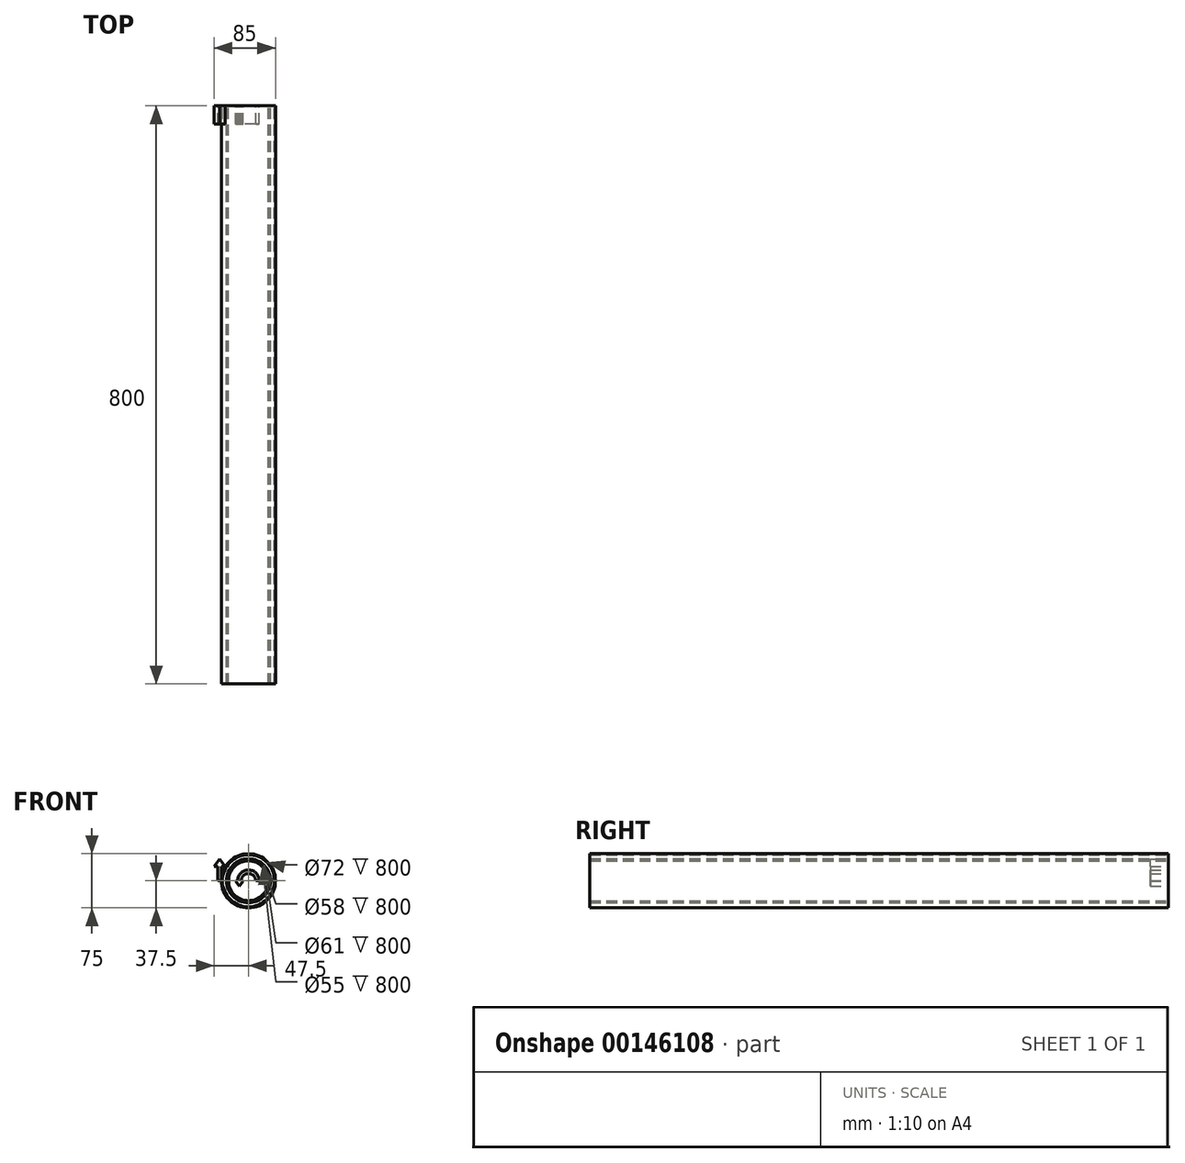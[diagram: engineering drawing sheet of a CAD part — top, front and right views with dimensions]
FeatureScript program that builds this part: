
annotation { "Feature Type Name" : "Feature", "Feature Type Description" : "" }
export const myFeature = defineFeature(function(context is Context, id is Id, definition is map)
    precondition{}
    {
        {
            var Q0;
            Q0=qCreatedBy(makeId("Front.planeOp"),FACE);
            var sketch = newSketch(context, id + "F0", { "sketchPlane" : qUnion([Q0])});
            skCircle(sketch, "E0", {"center": v(0, 0) * mm, "radius": 29 * mm});
            skCircle(sketch, "E1", {"center": v(0, 0) * mm, "radius": 30.5 * mm});
            skCircle(sketch, "E2", {"center": v(0, 0) * mm, "radius": 36 * mm});
            skCircle(sketch, "E3", {"center": v(0, 0) * mm, "radius": 37.5 * mm});
            skCircle(sketch, "E4", {"center": v(0, 0) * mm, "radius": 27.5 * mm});
            skLineSegment(sketch, "E5", {"start": v(0, 37.5) * mm, "end": v(-7.5, 52.5) * mm});
            skLineSegment(sketch, "E6", {"start": v(-7.5, 52.5) * mm, "end": v(-2.5, 52.5) * mm});
            skLineSegment(sketch, "E7", {"start": v(-2.5, 52.5) * mm, "end": v(-2.5, 67.5) * mm});
            skLineSegment(sketch, "E8", {"start": v(-2.5, 67.5) * mm, "end": v(2.5, 67.5) * mm});
            skLineSegment(sketch, "E9", {"start": v(2.5, 67.5) * mm, "end": v(2.5, 52.5) * mm});
            skLineSegment(sketch, "E10", {"start": v(2.5, 52.5) * mm, "end": v(7.5, 52.5) * mm});
            skLineSegment(sketch, "E11", {"start": v(7.5, 52.5) * mm, "end": v(0, 37.5) * mm});
            skLineSegment(sketch, "E12", {"start": v(0, 37.5) * mm, "end": v(0, 39.7) * mm, "construction": true});
            skSolve(sketch);
        }
        {
            var Q0;
            Q0=makeQuery(id+"F0.imprint","IMPRINT",FACE,{"disambiguationData":[TD([[makeQuery(id+"F0.imprint","IMPRINT",EDGE,{"derivedFrom":sQuery(id+"F0.wireOp",EDGE,"E0")}),1.0]])]});
            extrude(context, id + "F1", {"entities" : qUnion([Q0]), "depth" : 800 * mm});
        }
        {
            var Q0;
            Q0=makeQuery(id+"F0.imprint","IMPRINT",FACE,{"disambiguationData":[TD([[makeQuery(id+"F0.imprint","IMPRINT",EDGE,{"derivedFrom":sQuery(id+"F0.wireOp",EDGE,"E0")}),-1.0]])]});
            var Q1;
            Q1=makeQuery(id+"F1.opExtrude","CAP_FACE",FACE,{"disambiguationData":[OSD([sQuery(id+"F0.wireOp",EDGE,"E0"),sQuery(id+"F0.wireOp",EDGE,"E4")])],"isStart":false});
            var Q2;
            Q2=makeQuery(id+"F1.opExtrude","SWEPT_BODY",BODY,{"disambiguationData":[OSD([sQuery(id+"F0.wireOp",EDGE,"E0"),sQuery(id+"F0.wireOp",EDGE,"E4")])]});
            extrude(context, id + "F2", {"entities" : qUnion([Q0]), "endBound" : BoundingType.UP_TO_SURFACE, "endBoundEntityFace" : qUnion([Q1]), "endBoundEntityBody" : qUnion([Q2]), "depth" : 1660 * mm});
        }
        {
            var Q0;
            Q0=makeQuery(id+"F0.imprint","IMPRINT",FACE,{"disambiguationData":[TD([[makeQuery(id+"F0.imprint","IMPRINT",EDGE,{"derivedFrom":sQuery(id+"F0.wireOp",EDGE,"E1")}),-1.0]])]});
            var Q1;
            Q1=makeQuery(id+"F1.opExtrude","CAP_FACE",FACE,{"disambiguationData":[OSD([sQuery(id+"F0.wireOp",EDGE,"E0"),sQuery(id+"F0.wireOp",EDGE,"E4")])],"isStart":false});
            extrude(context, id + "F3", {"entities" : qUnion([Q0]), "endBound" : BoundingType.UP_TO_SURFACE, "endBoundEntityFace" : qUnion([Q1]), "depth" : 25 * mm});
        }
        {
            var Q0;
            Q0=makeQuery(id+"F0.imprint","IMPRINT",FACE,{"disambiguationData":[TD([[makeQuery(id+"F0.imprint","IMPRINT",EDGE,{"derivedFrom":sQuery(id+"F0.wireOp",EDGE,"E2")}),-1.0]])]});
            var Q1;
            Q1=makeQuery(id+"F3.opExtrude","CAP_FACE",FACE,{"disambiguationData":[OSD([sQuery(id+"F0.wireOp",EDGE,"E1"),sQuery(id+"F0.wireOp",EDGE,"E2")])],"isStart":false});
            extrude(context, id + "F4", {"entities" : qUnion([Q0]), "endBound" : BoundingType.UP_TO_SURFACE, "endBoundEntityFace" : qUnion([Q1]), "depth" : 25 * mm});
        }
        {
            var Q0;
            Q0=qCreatedBy(makeId("Front.planeOp"),FACE);
            var sketch = newSketch(context, id + "F5", { "sketchPlane" : qUnion([Q0])});
            skArc(sketch, "E13", {"start": v(15, 0.26) * mm, "mid": v(-0.26, 15) * mm, "end": v(-15, -0.26) * mm});
            skArc(sketch, "E14", {"start": v(10, 0.17) * mm, "mid": v(-0.17, 10) * mm, "end": v(-10, -0.17) * mm});
            skLineSegment(sketch, "E15", {"start": v(0, 0) * mm, "end": v(10, 0.17) * mm, "construction": true});
            skLineSegment(sketch, "E16", {"start": v(10, 0.17) * mm, "end": v(15, 0.26) * mm});
            skLineSegment(sketch, "E17", {"start": v(0, 0) * mm, "end": v(6.01, 0) * mm, "construction": true});
            skPoint(sketch, "E18.orphan", {"position": v(10, 0) * mm});
            skPoint(sketch, "E19.orphan", {"position": v(15, 0) * mm});
            skLineSegment(sketch, "E20", {"start": v(0, 0) * mm, "end": v(-10, -0.17) * mm, "construction": true});
            skPoint(sketch, "E21.orphan", {"position": v(-15, 0) * mm});
            skPoint(sketch, "E22.orphan", {"position": v(-10, 0) * mm});
            skLineSegment(sketch, "E23", {"start": v(-15, -0.26) * mm, "end": v(-17.5, -0.3) * mm});
            skLineSegment(sketch, "E24", {"start": v(-17.5, -0.3) * mm, "end": v(-12.38, -7.22) * mm});
            skLineSegment(sketch, "E25", {"start": v(-12.38, -7.22) * mm, "end": v(-7.5, -0.13) * mm});
            skLineSegment(sketch, "E26", {"start": v(-15, -0.26) * mm, "end": v(-10, -0.17) * mm, "construction": true});
            skLineSegment(sketch, "E27", {"start": v(-12.5, -0.22) * mm, "end": v(-12.38, -7.22) * mm, "construction": true});
            skLineSegment(sketch, "E28", {"start": v(-7.5, -0.13) * mm, "end": v(-10, -0.17) * mm});
            skSolve(sketch);
        }
        {
            var Q0;
            Q0=qSketchRegion(id+"F5",true);
            extrude(context, id + "F6", {"entities" : qUnion([Q0]), "depth" : 25 * mm});
        }
        {
            var Q0;
            Q0=qCreatedBy(makeId("Front.planeOp"),FACE);
            var sketch = newSketch(context, id + "F7", { "sketchPlane" : qUnion([Q0])});
            skLineSegment(sketch, "E29", {"start": v(-37.5, 20) * mm, "end": v(-37.5, 0) * mm});
            skLineSegment(sketch, "E30", {"start": v(-37.5, 20) * mm, "end": v(-32.5, 20) * mm});
            skLineSegment(sketch, "E31", {"start": v(-32.5, 20) * mm, "end": v(-40, 30) * mm});
            skLineSegment(sketch, "E32", {"start": v(-40, 30) * mm, "end": v(-47.5, 20) * mm});
            skLineSegment(sketch, "E33", {"start": v(-47.5, 20) * mm, "end": v(-42.5, 20) * mm});
            skLineSegment(sketch, "E34", {"start": v(-42.5, 0) * mm, "end": v(-42.5, 20) * mm});
            skLineSegment(sketch, "E35", {"start": v(-42.5, 0) * mm, "end": v(-37.5, 0) * mm});
            skLineSegment(sketch, "E36", {"start": v(-40, 0) * mm, "end": v(-40, -22.08) * mm, "construction": true});
            skSolve(sketch);
        }
        {
            var Q0;
            Q0 = qSketchRegion(id + "F7", true);
            extrude(context, id + "F8", {"entities" : qUnion([Q0]), "depth" : 25 * mm});
        }
    });
